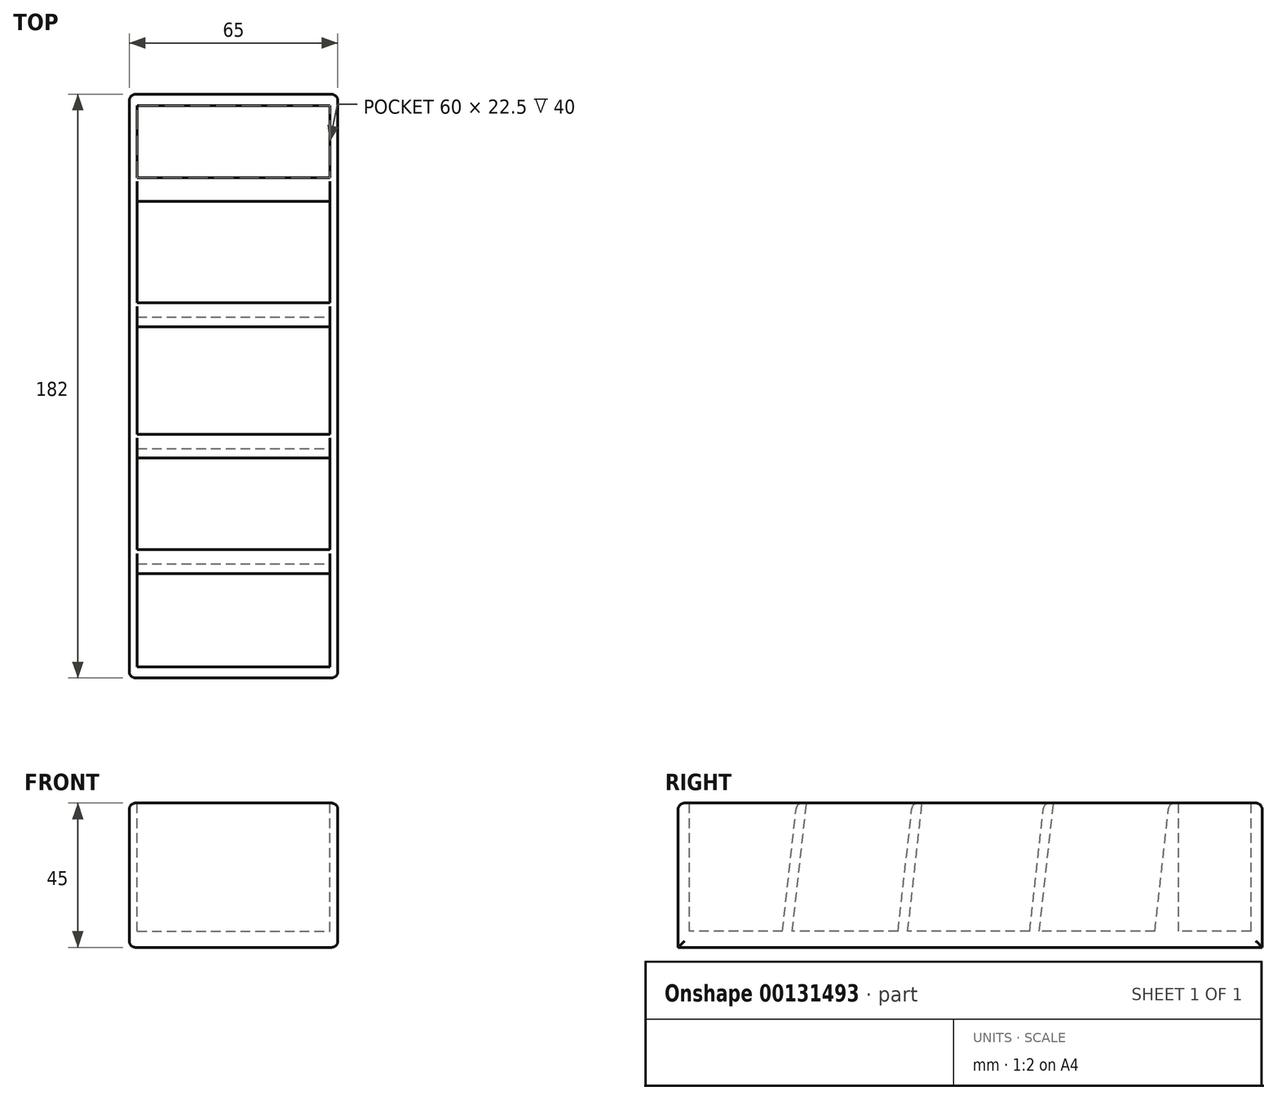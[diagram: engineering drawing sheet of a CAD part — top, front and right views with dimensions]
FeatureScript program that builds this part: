
annotation { "Feature Type Name" : "Feature", "Feature Type Description" : "" }
export const myFeature = defineFeature(function(context is Context, id is Id, definition is map)
    precondition{}
    {
        {
            var Q0;
            Q0=qCreatedBy(makeId("Top.planeOp"),FACE);
            var sketch = newSketch(context, id + "F0", { "sketchPlane" : qUnion([Q0])});
            skLineSegment(sketch, "E0.bottom", {"start": v(-32.5, 91) * mm, "end": v(32.5, 91) * mm});
            skLineSegment(sketch, "E0.top", {"start": v(-32.5, -91) * mm, "end": v(32.5, -91) * mm});
            skLineSegment(sketch, "E0.left", {"start": v(-32.5, 91) * mm, "end": v(-32.5, -91) * mm});
            skLineSegment(sketch, "E0.right", {"start": v(32.5, 91) * mm, "end": v(32.5, -91) * mm});
            skPoint(sketch, "E0.middle", {"position": v(0, 0) * mm});
            skSolve(sketch);
        }
        {
            var Q0;
            Q0 = qSketchRegion(id + "F0", true);
            extrude(context, id + "F1", {"entities" : qUnion([Q0]), "depth" : 45 * mm});
        }
        {
            var Q0;
            Q0=makeQuery(id+"F1.opExtrude","CAP_FACE",FACE,{"disambiguationData":[OSD([sQuery(id+"F0.wireOp",EDGE,"E0.bottom"),sQuery(id+"F0.wireOp",EDGE,"E0.top"),sQuery(id+"F0.wireOp",EDGE,"E0.left"),sQuery(id+"F0.wireOp",EDGE,"E0.right")])],"isStart":false});
            var sketch = newSketch(context, id + "F2", { "sketchPlane" : qUnion([Q0])});
            skPoint(sketch, "E1.middle", {"position": v(0, -3.13) * mm});
            skLineSegment(sketch, "E2.bottom", {"start": v(-30, 87.5) * mm, "end": v(30, 87.5) * mm});
            skLineSegment(sketch, "E2.top", {"start": v(-30, -87.5) * mm, "end": v(30, -87.5) * mm});
            skLineSegment(sketch, "E2.left", {"start": v(-30, 87.5) * mm, "end": v(-30, -87.5) * mm});
            skLineSegment(sketch, "E2.right", {"start": v(30, 87.5) * mm, "end": v(30, -87.5) * mm});
            skPoint(sketch, "E2.middle", {"position": v(0, 0) * mm});
            skSolve(sketch);
        }
        {
            var Q0;
            Q0 = qSketchRegion(id + "F2", true);
            extrude(context, id + "F3", {"entities" : qUnion([Q0]), "operationType" : NewBodyOperationType.REMOVE, "oppositeDirection" : true, "depth" : 40 * mm});
        }
        {
            var Q0;
            Q0=makeQuery(id+"F1.opExtrude","SWEPT_FACE",FACE,{"disambiguationData":[OSD([sQuery(id+"F0.wireOp",EDGE,"E0.right")])]});
            var sketch = newSketch(context, id + "F4", { "sketchPlane" : qUnion([Q0])});
            skLineSegment(sketch, "E3", {"start": v(-54, 45) * mm, "end": v(-59, 0) * mm});
            skLineSegment(sketch, "E4", {"start": v(-51, 45) * mm, "end": v(-56, 0) * mm});
            skLineSegment(sketch, "E5", {"start": v(-18, 45) * mm, "end": v(-23, 0) * mm});
            skLineSegment(sketch, "E6", {"start": v(-15, 45) * mm, "end": v(-20, 0) * mm});
            skLineSegment(sketch, "E7", {"start": v(-15, 45) * mm, "end": v(23, 45) * mm});
            skLineSegment(sketch, "E8", {"start": v(23, 45) * mm, "end": v(18, 0) * mm});
            skLineSegment(sketch, "E9", {"start": v(26, 45) * mm, "end": v(21, 0) * mm});
            skLineSegment(sketch, "E10", {"start": v(62, 45) * mm, "end": v(57, 0) * mm});
            skLineSegment(sketch, "E11", {"start": v(65, 45) * mm, "end": v(65, 0) * mm});
            skSolve(sketch);
        }
        {
            var Q0;
            {var subQ0=sQuery(id+"F4.wireOp",EDGE,"E3");Q0=makeQuery(id+"F4.imprint","IMPRINT",FACE,{"disambiguationData":[TD([[makeQuery(id+"F4.imprint","IMPRINT",EDGE,{"derivedFrom":subQ0}),1.0]])]});}
            var Q1;
            {var subQ0=sQuery(id+"F4.wireOp",EDGE,"E5");Q1=makeQuery(id+"F4.imprint","IMPRINT",FACE,{"disambiguationData":[TD([[makeQuery(id+"F4.imprint","IMPRINT",EDGE,{"derivedFrom":subQ0}),1.0]])]});}
            var Q2;
            {var subQ0=sQuery(id+"F4.wireOp",EDGE,"E8");Q2=makeQuery(id+"F4.imprint","IMPRINT",FACE,{"disambiguationData":[TD([[makeQuery(id+"F4.imprint","IMPRINT",EDGE,{"derivedFrom":subQ0}),1.0]])]});}
            var Q3;
            {var subQ0=sQuery(id+"F4.wireOp",EDGE,"E10");Q3=makeQuery(id+"F4.imprint","IMPRINT",FACE,{"disambiguationData":[TD([[makeQuery(id+"F4.imprint","IMPRINT",EDGE,{"derivedFrom":subQ0}),1.0]])]});}
            extrude(context, id + "F5", {"entities" : qUnion([Q0, Q1, Q2, Q3]), "operationType" : NewBodyOperationType.ADD, "oppositeDirection" : true, "depth" : 65 * mm});
        }
        {
            var Q0;
            Q0=makeQuery(id+"F1.opExtrude","SWEPT_FACE",FACE,{"disambiguationData":[OSD([sQuery(id+"F0.wireOp",EDGE,"E0.left")])]});
            var Q1;
            Q1=makeQuery(id+"F1.opExtrude","SWEPT_FACE",FACE,{"disambiguationData":[OSD([sQuery(id+"F0.wireOp",EDGE,"E0.right")])]});
            var Q2;
            Q2=makeQuery(id+"F1.opExtrude","CAP_EDGE",EDGE,{"disambiguationData":[OSD([sQuery(id+"F0.wireOp",EDGE,"E0.top")])],"isStart":false});
            var Q3;
            Q3=makeQuery(id+"F1.opExtrude","CAP_EDGE",EDGE,{"disambiguationData":[OSD([sQuery(id+"F0.wireOp",EDGE,"E0.bottom")])],"isStart":false});
            fillet(context, id + "F6", {"entities" : qUnion([Q0, Q1, Q2, Q3]), "radius" : 2 * mm, "tangentPropagation" : true, "allowEdgeOverflow" : false});
        }
        {
            var Q0;
            {var subQ0=sQuery(id+"F4.wireOp",EDGE,"E3");var subQ1=sQuery(id+"F0.wireOp",EDGE,"E0.right");Q0=makeQuery(id+"F5.opExtrude","SWEPT_EDGE",EDGE,{"disambiguationData":[OSD([subQ1,subQ0]),TDD([makeQuery(id+"F4.imprint","INTERSECT",VERTEX,{"derivedFrom":[makeQuery(id+"F1.opExtrude","CAP_EDGE",EDGE,{"disambiguationData":[OSD([subQ1])],"isStart":false}),subQ0]})])]});}
            var Q1;
            {var subQ0=sQuery(id+"F4.wireOp",EDGE,"E5");var subQ1=sQuery(id+"F0.wireOp",EDGE,"E0.right");Q1=makeQuery(id+"F5.opExtrude","SWEPT_EDGE",EDGE,{"disambiguationData":[OSD([subQ1,subQ0]),TDD([makeQuery(id+"F4.imprint","INTERSECT",VERTEX,{"derivedFrom":[makeQuery(id+"F1.opExtrude","CAP_EDGE",EDGE,{"disambiguationData":[OSD([subQ1])],"isStart":false}),subQ0]})])]});}
            var Q2;
            Q2=makeQuery(id+"F5.opExtrude","SWEPT_EDGE",EDGE,{"disambiguationData":[OSD([sQuery(id+"F0.wireOp",EDGE,"E0.right"),sQuery(id+"F4.wireOp",EDGE,"E7"),sQuery(id+"F4.wireOp",EDGE,"E8")])]});
            var Q3;
            {var subQ0=sQuery(id+"F4.wireOp",EDGE,"E10");var subQ1=sQuery(id+"F0.wireOp",EDGE,"E0.right");Q3=makeQuery(id+"F5.opExtrude","SWEPT_EDGE",EDGE,{"disambiguationData":[OSD([subQ1,subQ0]),TDD([makeQuery(id+"F4.imprint","INTERSECT",VERTEX,{"derivedFrom":[makeQuery(id+"F1.opExtrude","CAP_EDGE",EDGE,{"disambiguationData":[OSD([subQ1])],"isStart":false}),subQ0]})])]});}
            var Q4;
            Q4=makeQuery(id+"F3.boolean.opBoolean","COPY",EDGE,{"derivedFrom":makeQuery(id+"F3.opExtrude","CAP_EDGE",EDGE,{"disambiguationData":[OSD([sQuery(id+"F2.wireOp",EDGE,"E2.bottom")])],"isStart":true})});
            fillet(context, id + "F7", {"entities" : qUnion([Q0, Q1, Q2, Q3, Q4]), "radius" : 2 * mm, "tangentPropagation" : true, "allowEdgeOverflow" : false});
        }
    });
